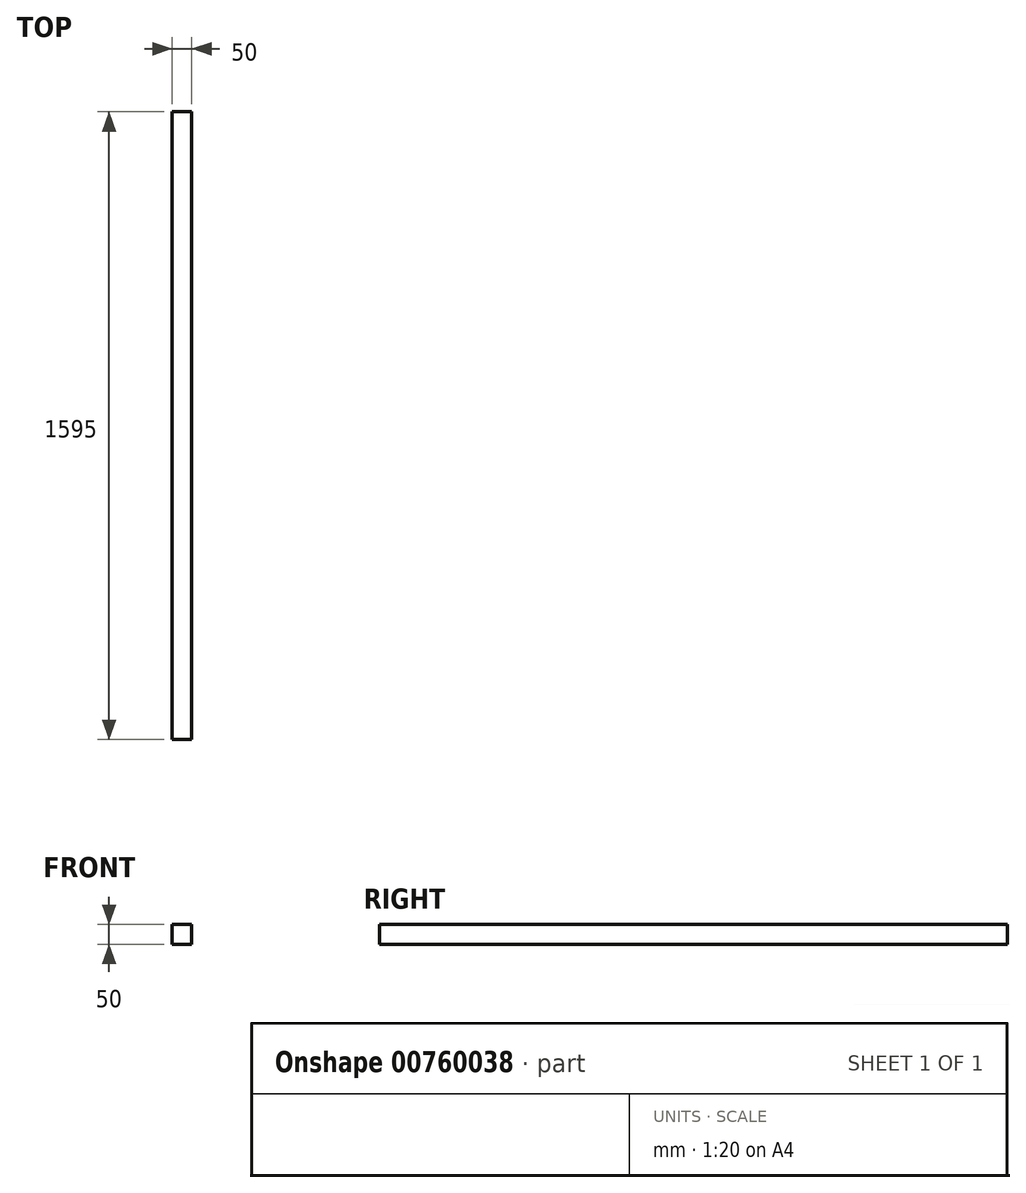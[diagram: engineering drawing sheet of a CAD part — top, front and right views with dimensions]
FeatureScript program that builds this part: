
annotation { "Feature Type Name" : "Feature", "Feature Type Description" : "" }
export const myFeature = defineFeature(function(context is Context, id is Id, definition is map)
    precondition{}
    {
        {
            var Q0;
            Q0=qCreatedBy(makeId("Right.planeOp"),FACE);
            var sketch = newSketch(context, id + "F0", { "sketchPlane" : qUnion([Q0])});
            skLineSegment(sketch, "E0", {"start": v(-797.5, 0) * mm, "end": v(797.5, 0) * mm});
            skSolve(sketch);
        }
        {
            var Q0;
            Q0=qCreatedBy(makeId("Front.planeOp"),FACE);
            cPlane(context, id + "F1", {"entities" : qUnion([Q0]), "cplaneType" : CPlaneType.OFFSET, "offset" : 797.5 * mm, "width" : 150 * mm, "height" : 150 * mm});
        }
        {
            var Q0;
            Q0=qCreatedBy(id+"F1.planeOp",FACE);
            var sketch = newSketch(context, id + "F2", { "sketchPlane" : qUnion([Q0])});
            skLineSegment(sketch, "E1.bottom", {"start": v(25, -25) * mm, "end": v(-25, -25) * mm});
            skLineSegment(sketch, "E1.top", {"start": v(25, 25) * mm, "end": v(-25, 25) * mm});
            skLineSegment(sketch, "E1.left", {"start": v(25, -25) * mm, "end": v(25, 25) * mm});
            skLineSegment(sketch, "E1.right", {"start": v(-25, -25) * mm, "end": v(-25, 25) * mm});
            skPoint(sketch, "E1.middle", {"position": v(0, 0) * mm});
            skSolve(sketch);
        }
        {
            var Q0;
            Q0=makeQuery(id+"F2.imprint","IMPRINT",FACE,{"disambiguationData":[TD([[makeQuery(id+"F2.imprint","IMPRINT",EDGE,{"derivedFrom":sQuery(id+"F2.wireOp",EDGE,"E1.bottom")}),-1.0]])]});
            var Q1;
            Q1=sQuery(id+"F0.wireOp",EDGE,"E0");
            sweep(context, id + "F3", {"profiles" : qUnion([Q0]), "path" : qUnion([Q1])});
        }
    });
